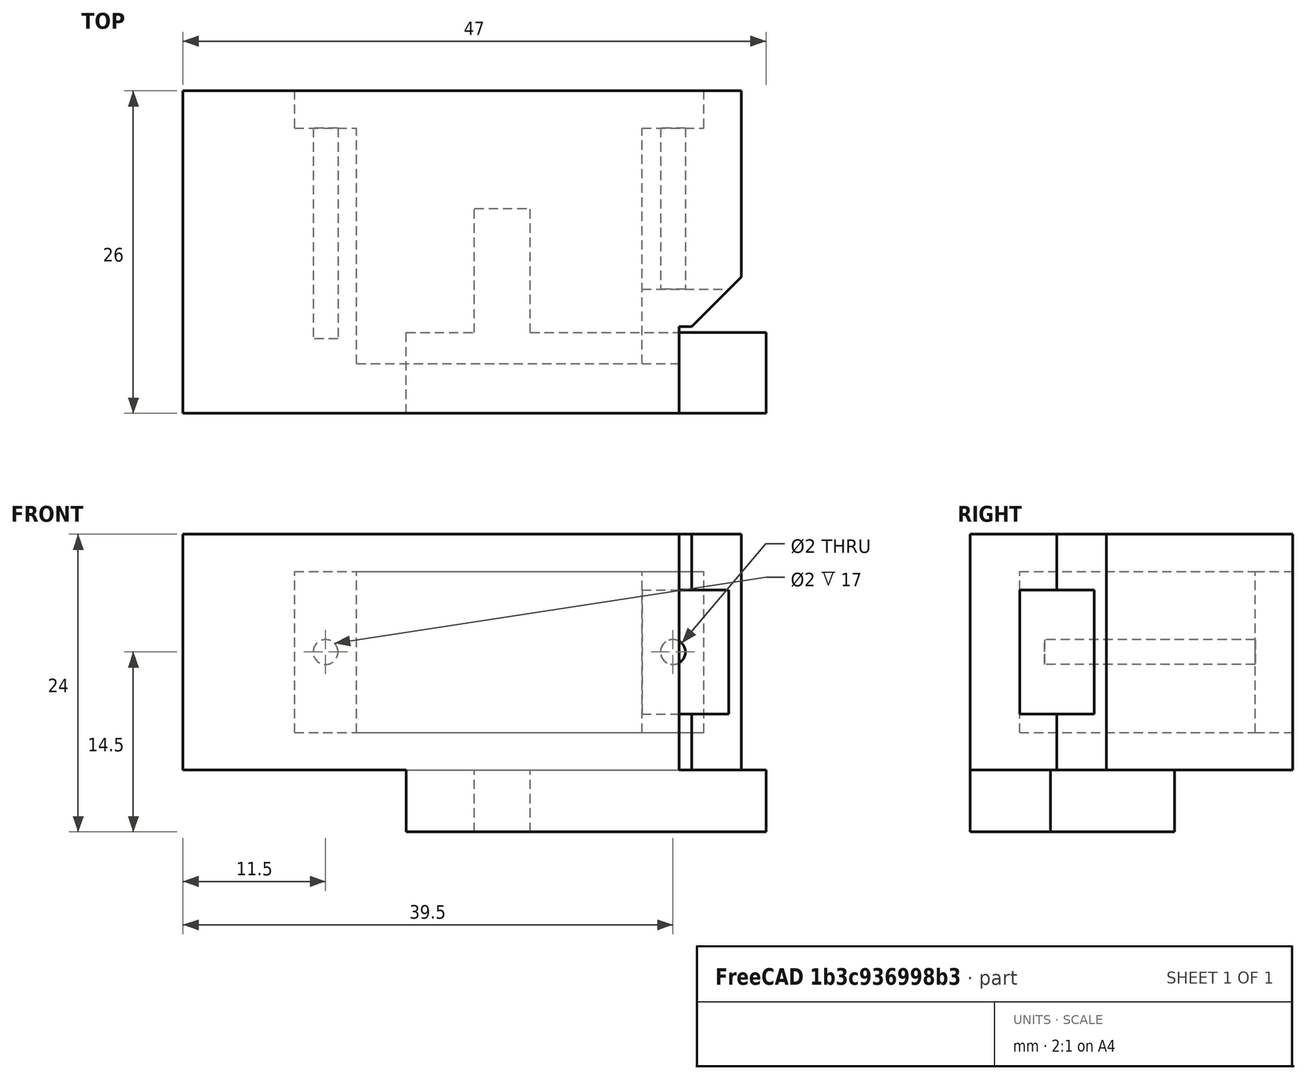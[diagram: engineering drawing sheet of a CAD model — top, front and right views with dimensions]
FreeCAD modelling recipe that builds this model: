
FCSTD DOCUMENT  (FreeCAD 0.15R4671 (Git))
Label: Sujeccion_servo
License: All rights reserved
LicenseURL: http://en.wikipedia.org/wiki/All_rights_reserved
objects: Part::Box×7, Part::MultiFuse×6, Part::Cylinder×2, Part::Chamfer×1, Part::Cut×1
note: 17 computed .brp shape members not serialized (recipe doc carries the construction recipe); baked Part::Feature solids carry a one-line shape summary decoded from their .brp

FEATURE [Part::Box] Box  label="Cubo"
  Height = 5
  Length = 29
  Placement = pos=(0,0,5) rot=(0,0,1;0rad)
  Width = 6.5
FEATURE [Part::Box] Box001  label="Cubo001"
  Height = 5
  Length = 4.5
  Placement = pos=(5.5,6.5,5) rot=(0,0,1;0rad)
  Width = 10
FEATURE [Part::MultiFuse] Fusion
  Shapes = -> [Box001,Box]
FEATURE [Part::Box] Box002  label="Cubo002"
  Height = 19
  Length = 40
  Placement = pos=(-18,0,10) rot=(0,0,1;0rad)
  Width = 26
FEATURE [Part::MultiFuse] Fusion001  label="Sujeccion"
  Shapes = -> [Box002,Fusion]
FEATURE [Part::Box] Box003  label="Cubo003"
  Height = 13
  Length = 23
  Placement = pos=(0,33,0) rot=(0,0,1;0rad)
  Width = 19
FEATURE [Part::Box] Box004  label="Cubo004"
  Height = 13
  Length = 33
  Placement = pos=(-5,52,0) rot=(0,0,1;0rad)
  Width = 3
FEATURE [Part::MultiFuse] Fusion002
  Shapes = -> [Box004,Box003]
FEATURE [Part::Cylinder] Cylinder  label="Cilindro"
  Angle = 360
  Height = 20
  Placement = pos=(-2.5,55,6.5) rot=(1,0,0;1.5708rad)
  Radius = 1
FEATURE [Part::Cylinder] Cylinder001  label="Cilindro001"
  Angle = 360
  Height = 20
  Placement = pos=(25.5,55,6.5) rot=(1,0,0;1.5708rad)
  Radius = 1
FEATURE [Part::MultiFuse] Fusion003  label="Servo_Model"
  Placement = pos=(-4,-1,13) rot=(0,0,1;0rad)
  Shapes = -> [Cylinder001,Cylinder,Fusion002]
FEATURE [Part::Box] Box005  label="Cubo005"
  Height = 19
  Length = 5
  Placement = pos=(22,7,10) rot=(0,0,1;0rad)
  Width = 19
FEATURE [Part::Chamfer] Chamfer
  Base = -> Box005
  Edges = 1 edges r=4: [Edge5]
FEATURE [Part::MultiFuse] Fusion004  label="Pieza"
  Shapes = -> [Fusion001,Chamfer]
FEATURE [Part::Box] Box006  label="Cubo006"
  Height = 10
  Length = 13
  Placement = pos=(17,32,14.5) rot=(0,0,1;0rad)
  Width = 6
FEATURE [Part::MultiFuse] Fusion005  label="Servo_Cable_model"
  Placement = pos=(0,-28,0) rot=(0,0,1;0rad)
  Shapes = -> [Box006,Fusion003]
FEATURE [Part::Cut] Cut  label="Pieza_sujeccion_Servo"
  Base = -> Fusion004
  Placement = pos=(0,0,-5) rot=(0,0,1;0rad)
  Tool = -> Fusion005
